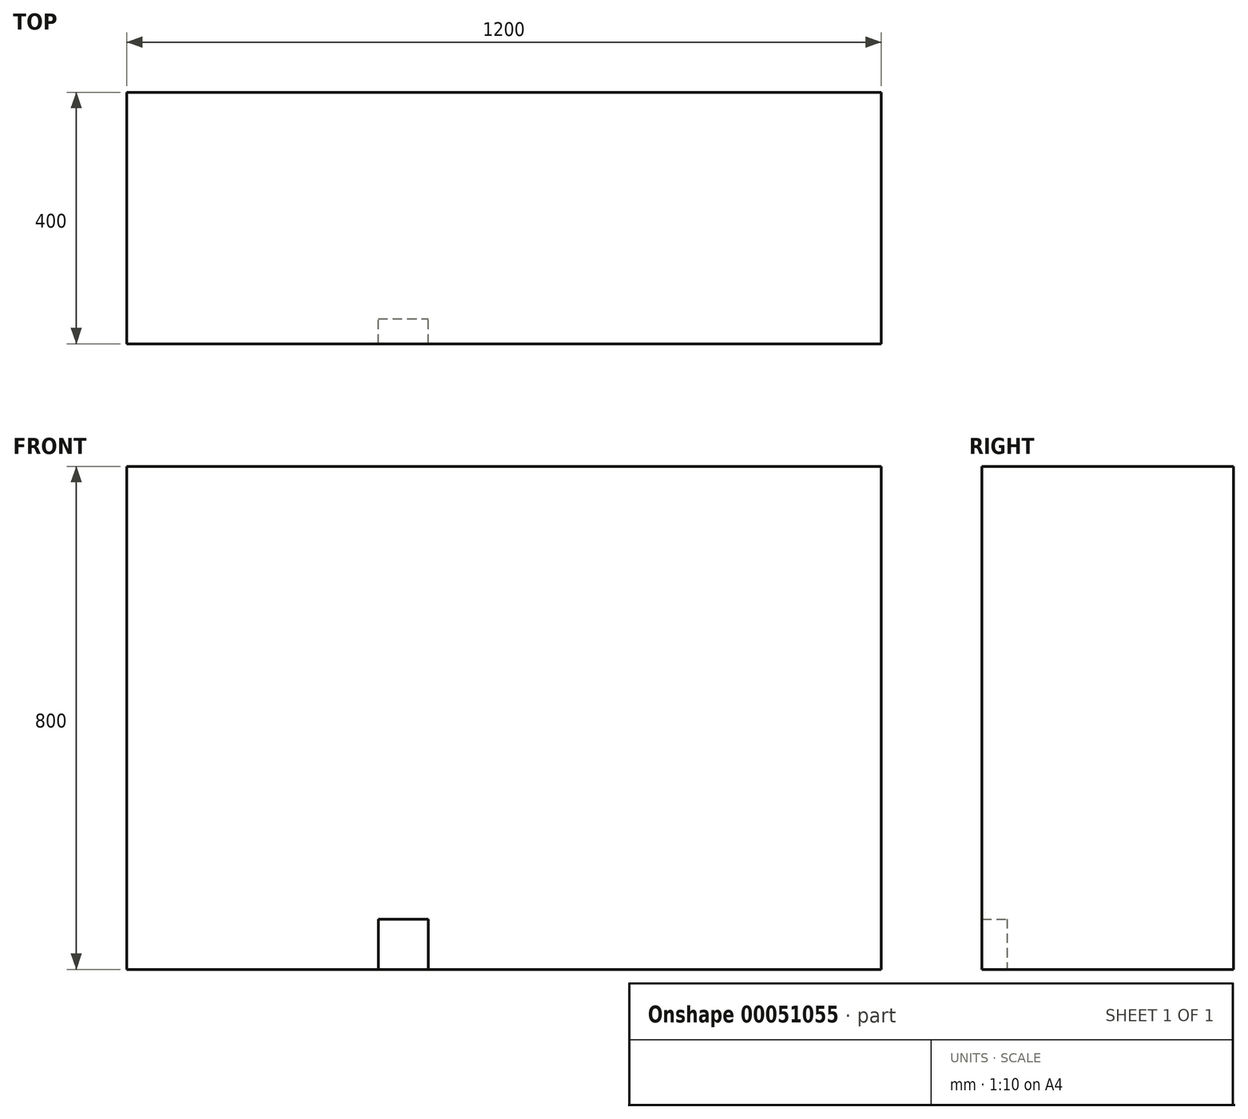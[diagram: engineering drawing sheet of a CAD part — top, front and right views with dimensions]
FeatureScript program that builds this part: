
annotation { "Feature Type Name" : "Feature", "Feature Type Description" : "" }
export const myFeature = defineFeature(function(context is Context, id is Id, definition is map)
    precondition{}
    {
        {
            var Q0;
            Q0=qCreatedBy(makeId("Top.planeOp"),FACE);
            var sketch = newSketch(context, id + "F0", { "sketchPlane" : qUnion([Q0])});
            skLineSegment(sketch, "E0.bottom", {"start": v(0, 0) * mm, "end": v(1200, 0) * mm});
            skLineSegment(sketch, "E0.top", {"start": v(0, 400) * mm, "end": v(1200, 400) * mm});
            skLineSegment(sketch, "E0.left", {"start": v(0, 0) * mm, "end": v(0, 400) * mm});
            skLineSegment(sketch, "E0.right", {"start": v(1200, 0) * mm, "end": v(1200, 400) * mm});
            skSolve(sketch);
        }
        {
            var Q0;
            Q0=qCreatedBy(makeId("Top.planeOp"),FACE);
            var sketch = newSketch(context, id + "F1", { "sketchPlane" : qUnion([Q0])});
            skLineSegment(sketch, "E1.bottom", {"start": v(400, 0) * mm, "end": v(480, 0) * mm});
            skLineSegment(sketch, "E1.top", {"start": v(400, 40) * mm, "end": v(480, 40) * mm});
            skLineSegment(sketch, "E1.left", {"start": v(400, 0) * mm, "end": v(400, 40) * mm});
            skLineSegment(sketch, "E1.right", {"start": v(480, 0) * mm, "end": v(480, 40) * mm});
            skSolve(sketch);
        }
        {
            var Q0;
            Q0=makeQuery(id+"F0.imprint","IMPRINT",FACE,{"disambiguationData":[TD([[makeQuery(id+"F0.imprint","IMPRINT",EDGE,{"derivedFrom":sQuery(id+"F0.wireOp",EDGE,"E0.bottom")}),1.0]])]});
            extrude(context, id + "F2", {"entities" : qUnion([Q0]), "depth" : 800 * mm});
        }
        {
            var Q0;
            Q0=makeQuery(id+"F1.imprint","IMPRINT",FACE,{"disambiguationData":[TD([[makeQuery(id+"F1.imprint","IMPRINT",EDGE,{"derivedFrom":sQuery(id+"F1.wireOp",EDGE,"E1.bottom")}),1.0]])]});
            extrude(context, id + "F3", {"entities" : qUnion([Q0]), "operationType" : NewBodyOperationType.REMOVE, "depth" : 80 * mm});
        }
    });
